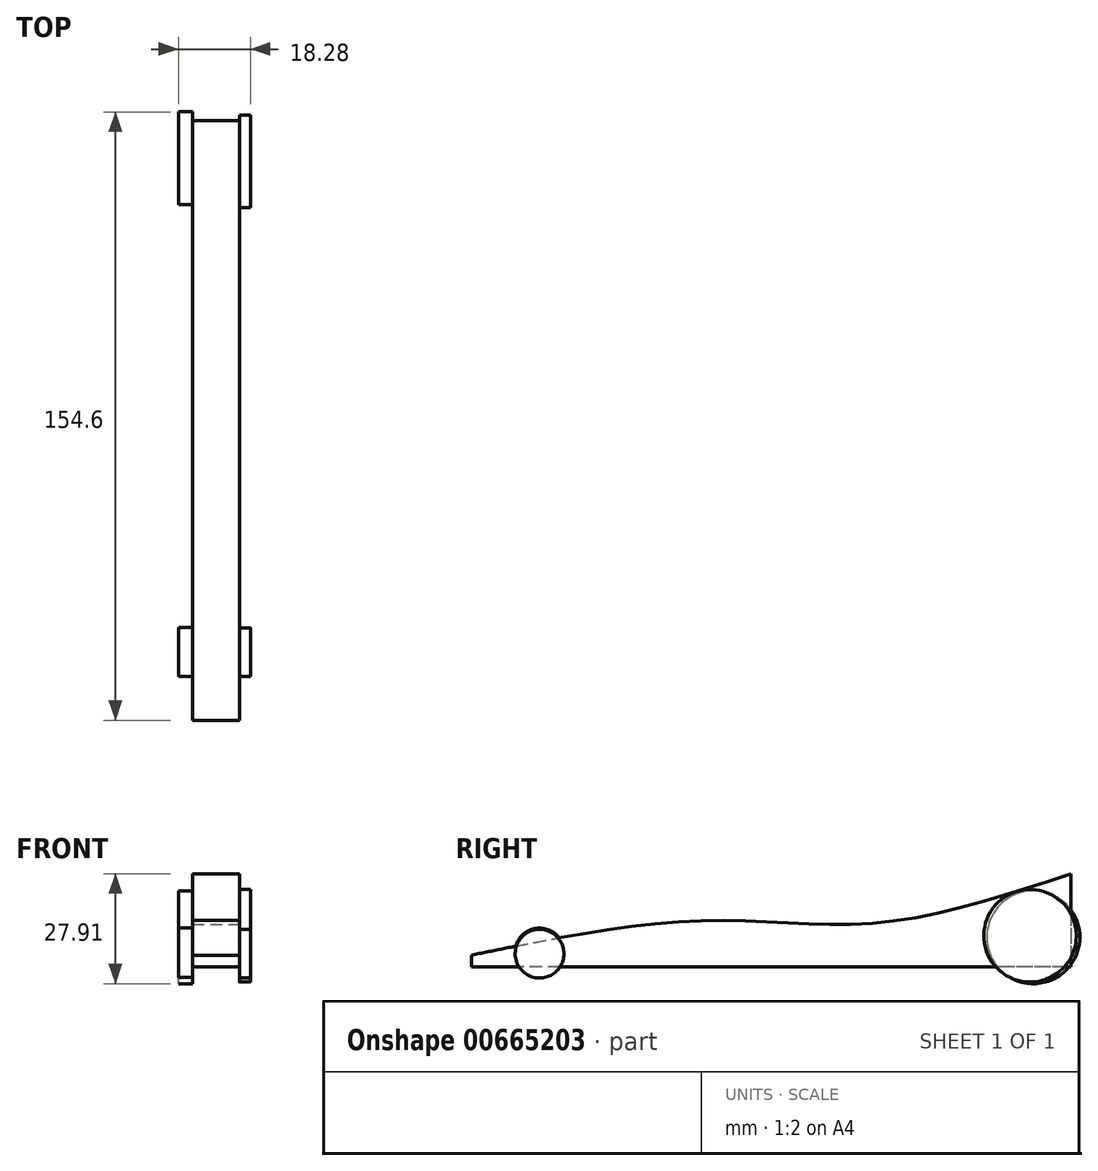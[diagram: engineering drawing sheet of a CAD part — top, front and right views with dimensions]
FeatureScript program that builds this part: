
annotation { "Feature Type Name" : "Feature", "Feature Type Description" : "" }
export const myFeature = defineFeature(function(context is Context, id is Id, definition is map)
    precondition{}
    {
        {
            var Q0;
            Q0=qCreatedBy(makeId("Right.planeOp"),FACE);
            var sketch = newSketch(context, id + "F0", { "sketchPlane" : qUnion([Q0])});
            skFitSpline(sketch, "E0", {"points": [v(-76.5, 2.98) * mm, v(-18.21, 11.72) * mm, v(26.56, 11.2) * mm, v(75.84, 23.65) * mm], "startDerivative": vector(169.02, 34.59) * mm, "endDerivative": vector(151.12, 49.94) * mm});
            skLineSegment(sketch, "E1", {"start": v(75.84, 23.65) * mm, "end": v(75.84, 0) * mm});
            skLineSegment(sketch, "E2", {"start": v(75.84, 0) * mm, "end": v(-76.5, 0) * mm});
            skLineSegment(sketch, "E3", {"start": v(-76.5, 0) * mm, "end": v(-76.5, 2.98) * mm});
            skSolve(sketch);
        }
        {
            var Q0;
            Q0=makeQuery(id+"F0.imprint","IMPRINT",FACE,{"disambiguationData":[TD([[makeQuery(id+"F0.imprint","IMPRINT",EDGE,{"derivedFrom":sQuery(id+"F0.wireOp",EDGE,"E0")}),-1.0]])]});
            extrude(context, id + "F1", {"entities" : qUnion([Q0]), "oppositeDirection" : true, "depth" : 11.94 * mm, "offsetDistance" : 25.4 * mm});
        }
        {
            var Q0;
            Q0=qCreatedBy(makeId("Right.planeOp"),FACE);
            var sketch = newSketch(context, id + "F2", { "sketchPlane" : qUnion([Q0])});
            skCircle(sketch, "E4", {"center": v(-59.16, 3.35) * mm, "radius": 6.19 * mm});
            skCircle(sketch, "E5", {"center": v(65.47, 7.9) * mm, "radius": 11.75 * mm});
            skSolve(sketch);
        }
        {
            var Q0;
            Q0=makeQuery(id+"F2.imprint","IMPRINT",FACE,{"disambiguationData":[TD([[makeQuery(id+"F2.imprint","IMPRINT",EDGE,{"derivedFrom":sQuery(id+"F2.wireOp",EDGE,"E4")}),1.0]])]});
            var Q1;
            Q1=makeQuery(id+"F2.imprint","IMPRINT",FACE,{"disambiguationData":[TD([[makeQuery(id+"F2.imprint","IMPRINT",EDGE,{"derivedFrom":sQuery(id+"F2.wireOp",EDGE,"E5")}),1.0]])]});
            extrude(context, id + "F3", {"entities" : qUnion([Q0, Q1]), "operationType" : NewBodyOperationType.ADD, "depth" : 2.8 * mm, "offsetDistance" : 25.4 * mm});
        }
        {
            var Q0;
            Q0=qCreatedBy(makeId("Right.planeOp"),FACE);
            cPlane(context, id + "F4", {"entities" : qUnion([Q0]), "cplaneType" : CPlaneType.OFFSET, "offset" : 11.94 * mm, "oppositeDirection" : true, "width" : 152.4 * mm, "height" : 152.4 * mm});
        }
        {
            var Q0;
            Q0=qCreatedBy(id+"F4.planeOp",FACE);
            var sketch = newSketch(context, id + "F5", { "sketchPlane" : qUnion([Q0])});
            skCircle(sketch, "E6", {"center": v(-59.15, 3.62) * mm, "radius": 6.25 * mm});
            skCircle(sketch, "E7", {"center": v(66.3, 7.55) * mm, "radius": 11.81 * mm});
            skSolve(sketch);
        }
        {
            var Q0;
            Q0=makeQuery(id+"F5.imprint","IMPRINT",FACE,{"disambiguationData":[TD([[makeQuery(id+"F5.imprint","IMPRINT",EDGE,{"derivedFrom":sQuery(id+"F5.wireOp",EDGE,"E7")}),1.0]])]});
            var Q1;
            Q1=makeQuery(id+"F5.imprint","IMPRINT",FACE,{"disambiguationData":[TD([[makeQuery(id+"F5.imprint","IMPRINT",EDGE,{"derivedFrom":sQuery(id+"F5.wireOp",EDGE,"E6")}),1.0]])]});
            extrude(context, id + "F6", {"entities" : qUnion([Q0, Q1]), "operationType" : NewBodyOperationType.ADD, "oppositeDirection" : true, "depth" : 3.56 * mm, "offsetDistance" : 25.4 * mm});
        }
    });
